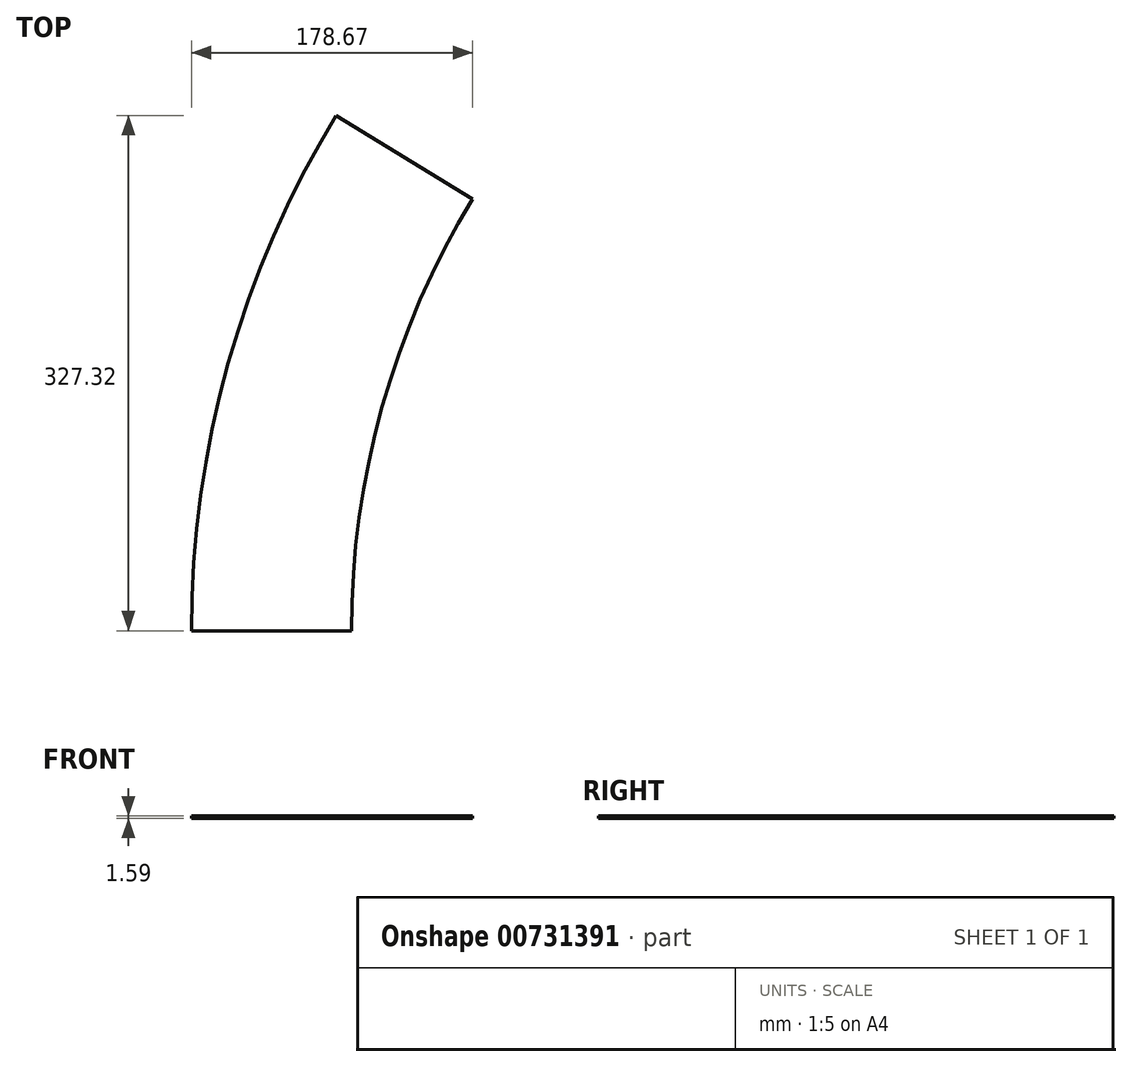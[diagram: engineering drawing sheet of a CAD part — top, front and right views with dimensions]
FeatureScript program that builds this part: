
annotation { "Feature Type Name" : "Feature", "Feature Type Description" : "" }
export const myFeature = defineFeature(function(context is Context, id is Id, definition is map)
    precondition{}
    {
        {
            var Q0;
            Q0=qCreatedBy(makeId("Top.planeOp"),FACE);
            var sketch = newSketch(context, id + "F0", { "sketchPlane" : qUnion([Q0])});
            skArc(sketch, "E0", {"start": v(-536.73, 327.32) * mm, "mid": v(-605.24, 170) * mm, "end": v(-628.66, 0) * mm});
            skArc(sketch, "E1", {"start": v(-449.99, 274.42) * mm, "mid": v(-507.43, 142.52) * mm, "end": v(-527.06, 0) * mm});
            skLineSegment(sketch, "E2", {"start": v(-527.06, 0) * mm, "end": v(-628.66, 0) * mm});
            skLineSegment(sketch, "E3", {"start": v(-449.99, 274.42) * mm, "end": v(-536.73, 327.32) * mm});
            skSolve(sketch);
        }
        {
            var Q0;
            Q0 = qSketchRegion(id + "F0", true);
            extrude(context, id + "F1", {"entities" : qUnion([Q0]), "depth" : 1.59 * mm, "offsetDistance" : 25.4 * mm});
        }
    });
